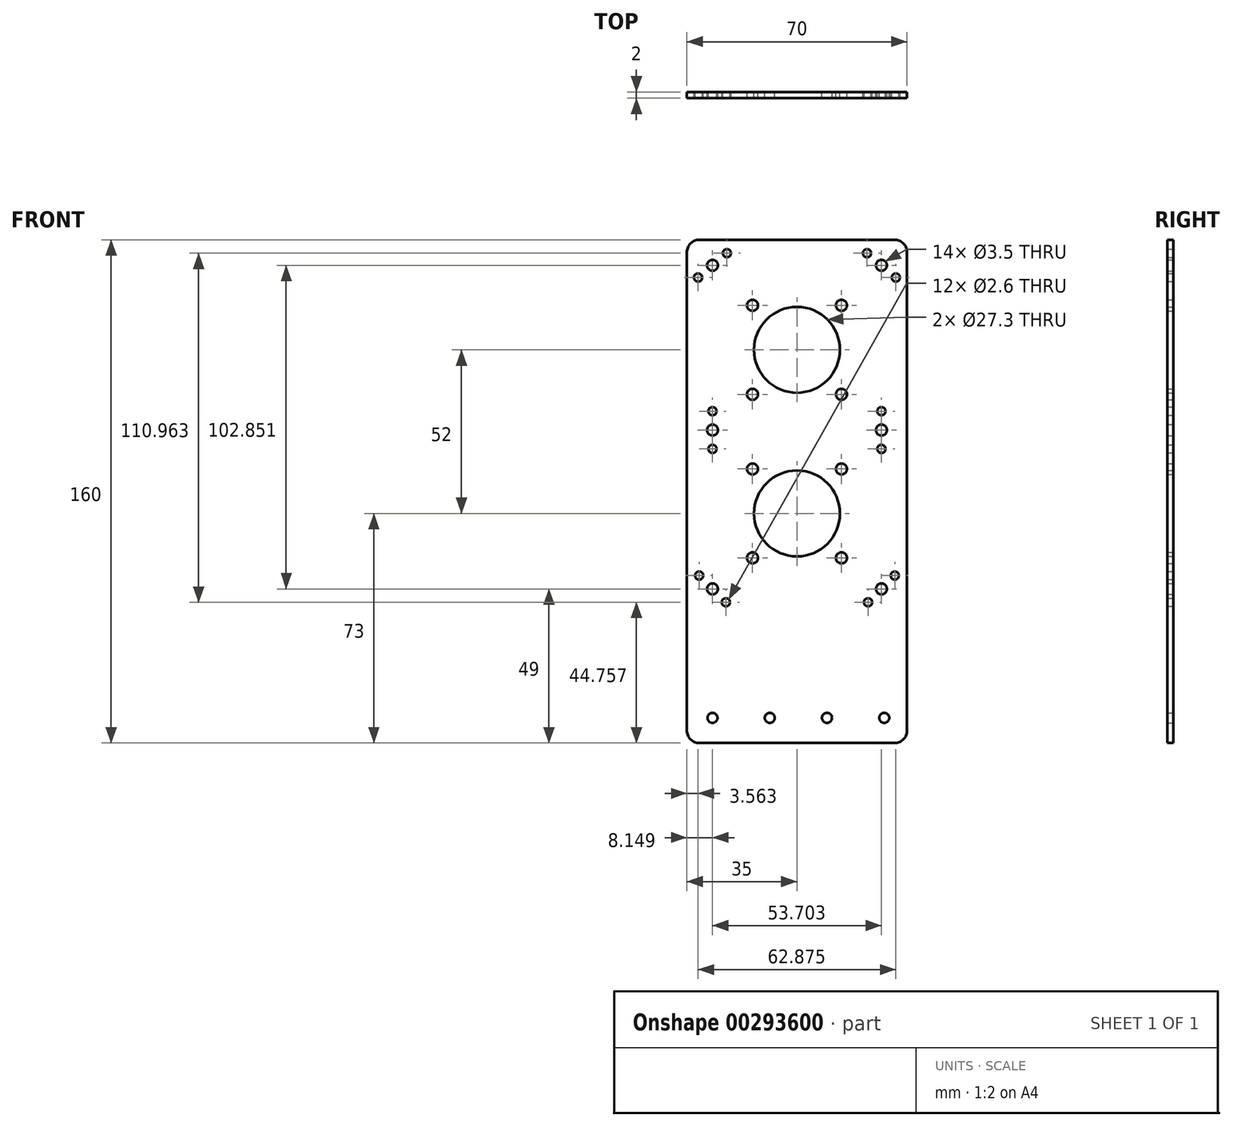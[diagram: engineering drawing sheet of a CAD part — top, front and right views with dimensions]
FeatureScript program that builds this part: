
annotation { "Feature Type Name" : "Feature", "Feature Type Description" : "" }
export const myFeature = defineFeature(function(context is Context, id is Id, definition is map)
    precondition{}
    {
        {
            var Q0;
            Q0=qCreatedBy(makeId("Front.planeOp"),FACE);
            var sketch = newSketch(context, id + "F0", { "sketchPlane" : qUnion([Q0])});
            skCircle(sketch, "E0", {"center": v(0, 0) * mm, "radius": 13.65 * mm});
            skLineSegment(sketch, "E1", {"start": v(0, 0) * mm, "end": v(16.49, 16.49) * mm, "construction": true});
            skCircle(sketch, "E2", {"center": v(0, 0) * mm, "radius": 20 * mm, "construction": true});
            skCircle(sketch, "E3", {"center": v(14.14, 14.14) * mm, "radius": 1.75 * mm});
            skPoint(sketch, "E4.center", {"position": v(1, 1) * mm});
            skLineSegment(sketch, "E5", {"start": v(0, 59.6) * mm, "end": v(0, -99.24) * mm, "construction": true});
            skLineSegment(sketch, "E6", {"start": v(-36.68, 0) * mm, "end": v(42.66, 0) * mm, "construction": true});
            skLineSegment(sketch, "E7", {"start": v(-35, 35) * mm, "end": v(-35, -125) * mm});
            skLineSegment(sketch, "E8", {"start": v(-35, -125) * mm, "end": v(35, -125) * mm});
            skLineSegment(sketch, "E9", {"start": v(35, -125) * mm, "end": v(35, 35) * mm});
            skLineSegment(sketch, "E10", {"start": v(35, 35) * mm, "end": v(-35, 35) * mm});
            skLineSegment(sketch, "E11", {"start": v(0, 0) * mm, "end": v(-35, 35) * mm});
            skCircle(sketch, "E12", {"center": v(-26.85, 26.85) * mm, "radius": 1.75 * mm});
            skLineSegment(sketch, "E13", {"start": v(-26.85, 26.85) * mm, "end": v(-36.02, 19.11) * mm, "construction": true});
            skLineSegment(sketch, "E14", {"start": v(-26.85, 26.85) * mm, "end": v(-17.68, 34.59) * mm, "construction": true});
            skCircle(sketch, "E15", {"center": v(-22.27, 30.72) * mm, "radius": 1.3 * mm});
            skCircle(sketch, "E16", {"center": v(-31.44, 22.98) * mm, "radius": 1.3 * mm});
            skCircle(sketch, "E17.MirrorC", {"center": v(22.27, 30.72) * mm, "radius": 1.3 * mm});
            skCircle(sketch, "E18.MirrorC", {"center": v(26.85, 26.85) * mm, "radius": 1.75 * mm});
            skCircle(sketch, "E19.MirrorC", {"center": v(31.44, 22.98) * mm, "radius": 1.3 * mm});
            skCircle(sketch, "E20", {"center": v(0, -52) * mm, "radius": 13.65 * mm});
            skLineSegment(sketch, "E21", {"start": v(0, -52) * mm, "end": v(22.27, -29.73) * mm, "construction": true});
            skCircle(sketch, "E22", {"center": v(0, -52) * mm, "radius": 20 * mm, "construction": true});
            skCircle(sketch, "E23", {"center": v(14.14, -37.86) * mm, "radius": 1.75 * mm});
            skLineSegment(sketch, "E24", {"start": v(26.85, 26.85) * mm, "end": v(26.85, -96.93) * mm, "construction": true});
            skLineSegment(sketch, "E25", {"start": v(-26.85, 26.85) * mm, "end": v(-26.85, -97.67) * mm, "construction": true});
            skCircle(sketch, "E26", {"center": v(-26.85, -76) * mm, "radius": 1.75 * mm});
            skLineSegment(sketch, "E27", {"start": v(-31.53, -71.32) * mm, "end": v(-20.48, -82.38) * mm, "construction": true});
            skCircle(sketch, "E28", {"center": v(-22.6, -80.24) * mm, "radius": 1.3 * mm});
            skCircle(sketch, "E29", {"center": v(-31.1, -71.76) * mm, "radius": 1.3 * mm});
            skLineSegment(sketch, "E30", {"start": v(-35.4, -117) * mm, "end": v(41.52, -117) * mm, "construction": true});
            skCircle(sketch, "E31", {"center": v(-26.85, -117) * mm, "radius": 1.6 * mm});
            skCircle(sketch, "E32.1.0.0", {"center": v(-8.65, -117) * mm, "radius": 1.6 * mm});
            skCircle(sketch, "E32.2.0.0", {"center": v(9.55, -117) * mm, "radius": 1.6 * mm});
            skCircle(sketch, "E32.3.0.0", {"center": v(27.75, -117) * mm, "radius": 1.6 * mm});
            skLineSegment(sketch, "E32.direction1", {"start": v(-26.85, -117) * mm, "end": v(-8.65, -117) * mm, "construction": true});
            skCircle(sketch, "E33.MirrorC", {"center": v(22.6, -80.24) * mm, "radius": 1.3 * mm});
            skCircle(sketch, "E34.MirrorC", {"center": v(26.85, -76) * mm, "radius": 1.75 * mm});
            skCircle(sketch, "E35.MirrorC", {"center": v(31.1, -71.76) * mm, "radius": 1.3 * mm});
            skLineSegment(sketch, "E36", {"start": v(-35, -25.5) * mm, "end": v(35, -25.5) * mm, "construction": true});
            skCircle(sketch, "E37", {"center": v(26.85, -25.5) * mm, "radius": 1.75 * mm});
            skCircle(sketch, "E38", {"center": v(26.85, -31.5) * mm, "radius": 1.3 * mm});
            skCircle(sketch, "E39", {"center": v(26.85, -19.5) * mm, "radius": 1.3 * mm});
            skCircle(sketch, "E40.MirrorC", {"center": v(-26.85, -19.5) * mm, "radius": 1.3 * mm});
            skCircle(sketch, "E41.MirrorC", {"center": v(-26.85, -25.5) * mm, "radius": 1.75 * mm});
            skCircle(sketch, "E42.MirrorC", {"center": v(-26.85, -31.5) * mm, "radius": 1.3 * mm});
            skLineSegment(sketch, "E43", {"start": v(-35, -100) * mm, "end": v(35, -100) * mm, "construction": true});
            skCircle(sketch, "E44.1.0", {"center": v(-14.14, 14.14) * mm, "radius": 1.75 * mm});
            skCircle(sketch, "E44.2.0", {"center": v(-14.14, -14.14) * mm, "radius": 1.75 * mm});
            skCircle(sketch, "E44.3.0", {"center": v(14.14, -14.14) * mm, "radius": 1.75 * mm});
            skCircle(sketch, "E45.1.0", {"center": v(-14.14, -37.86) * mm, "radius": 1.75 * mm});
            skCircle(sketch, "E45.2.0", {"center": v(-14.14, -66.14) * mm, "radius": 1.75 * mm});
            skCircle(sketch, "E45.3.0", {"center": v(14.14, -66.14) * mm, "radius": 1.75 * mm});
            skLineSegment(sketch, "E46", {"start": v(0, -99.24) * mm, "end": v(17.07, 63.12) * mm, "construction": true});
            skSolve(sketch);
        }
        {
            var Q0;
            Q0=makeQuery(id+"F0.imprint","IMPRINT",FACE,{"disambiguationData":[TD([[makeQuery(id+"F0.imprint","IMPRINT",EDGE,{"derivedFrom":sQuery(id+"F0.wireOp",EDGE,"E0")}),-1.0]])]});
            extrude(context, id + "F1", {"entities" : qUnion([Q0]), "depth" : 2 * mm});
        }
        {
            var Q0;
            Q0=makeQuery(id+"F1.opExtrude","SWEPT_EDGE",EDGE,{"disambiguationData":[OSD([sQuery(id+"F0.wireOp",EDGE,"E9"),sQuery(id+"F0.wireOp",EDGE,"E10")])]});
            var Q1;
            Q1=makeQuery(id+"F1.opExtrude","SWEPT_EDGE",EDGE,{"disambiguationData":[OSD([sQuery(id+"F0.wireOp",EDGE,"E8"),sQuery(id+"F0.wireOp",EDGE,"E9")])]});
            var Q2;
            Q2=makeQuery(id+"F1.opExtrude","SWEPT_EDGE",EDGE,{"disambiguationData":[OSD([sQuery(id+"F0.wireOp",EDGE,"E7"),sQuery(id+"F0.wireOp",EDGE,"E10")])]});
            var Q3;
            Q3=makeQuery(id+"F1.opExtrude","SWEPT_EDGE",EDGE,{"disambiguationData":[OSD([sQuery(id+"F0.wireOp",EDGE,"E7"),sQuery(id+"F0.wireOp",EDGE,"E8")])]});
            fillet(context, id + "F2", {"entities" : qUnion([Q0, Q1, Q2, Q3]), "radius" : 4 * mm, "tangentPropagation" : true, "allowEdgeOverflow" : false});
        }
    });
